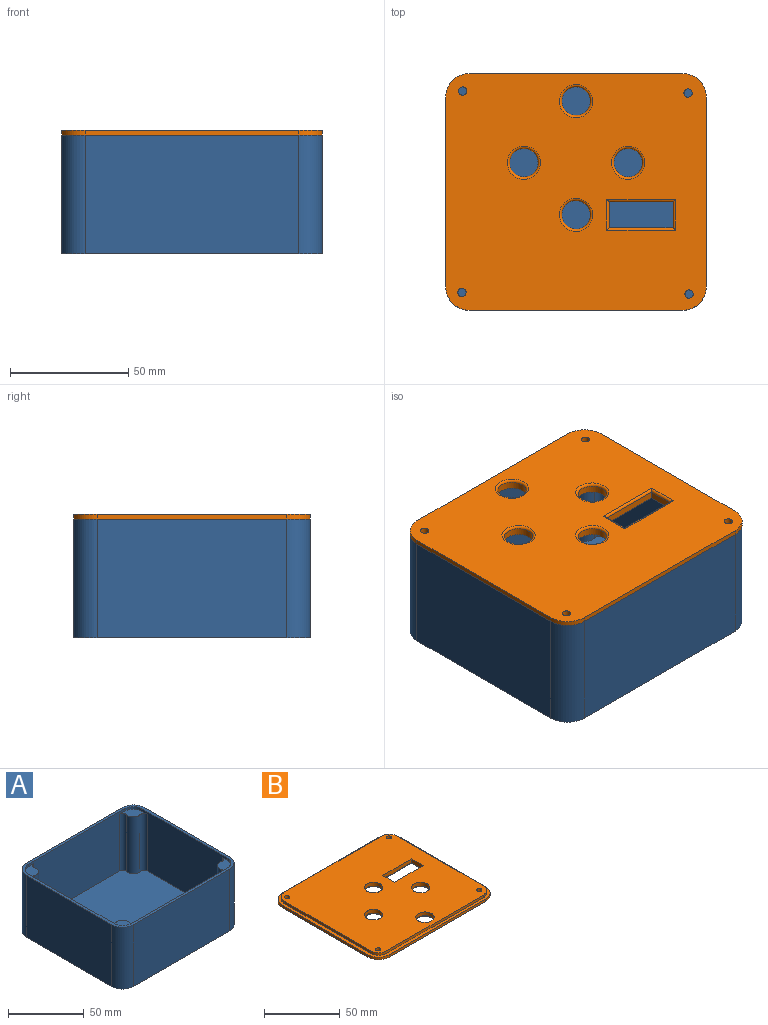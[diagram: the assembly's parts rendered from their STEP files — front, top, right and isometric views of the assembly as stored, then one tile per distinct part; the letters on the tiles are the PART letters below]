
ASSEMBLY  parts=2 mates=1
PART A: 35 faces, bbox 110x100x50 mm
  f0: cylinder r=8mm len=8mm, axis (0,0,-1), area 25.1mm2, adj f2,f13,f14,f29
  f1: cylinder r=8mm len=8mm, axis (0,0,-1), area 25.1mm2, adj f2,f16,f17,f19
  f2: plane 110x100mm, normal (0,0,1), area 793.1mm2, adj f0,f1,f3,f4,f5,f6,f7,f8
  f3: cylinder r=10mm len=50mm, axis (0,0,-1), area 785.4mm2, adj f2,f4,f10,f11
  f4: plane 90x50mm, normal (0,-1,0), area 4500mm2, adj f2,f3,f5,f11
  f5: cylinder r=10mm len=50mm, axis (0,0,-1), area 785.4mm2, adj f2,f4,f6,f11
  f6: plane 80x50mm, normal (1,0,0), area 4000mm2, adj f2,f5,f7,f11
  f7: cylinder r=10mm len=50mm, axis (0,0,-1), area 785.4mm2, adj f2,f6,f8,f11
  f8: plane 90x50mm, normal (0,1,0), area 4500mm2, adj f2,f7,f9,f11
  f9: cylinder r=10mm len=50mm, axis (0,0,-1), area 785.4mm2, adj f2,f8,f10,f11
  f10: plane 80x50mm, normal (-1,0,0), area 4000mm2, adj f2,f3,f9,f11
  f11: plane 110x100mm, normal (0,0,-1), area 10914.2mm2, adj f3,f4,f5,f6,f7,f8,f9,f10
  f12: cylinder r=8mm len=8mm, axis (0,0,-1), area 25.1mm2, adj f2,f13,f17,f27
  f13: plane 90x48mm, normal (0,1,0), area 3871.8mm2, adj f0,f2,f12,f18,f27,f29,f31,f34
  f14: plane 80x48mm, normal (-1,0,0), area 3391.8mm2, adj f0,f2,f15,f18,f23,f26,f29,f32
  f15: cylinder r=8mm len=8mm, axis (0,0,-1), area 25.1mm2, adj f2,f14,f16,f23
  f16: plane 90x48mm, normal (0,-1,0), area 3871.8mm2, adj f1,f2,f15,f18,f19,f21,f23,f25
  f17: plane 80x48mm, normal (1,0,0), area 3391.8mm2, adj f1,f2,f12,f18,f19,f22,f27,f33
  f18: plane 106x96mm, normal (0,0,1), area 9777.8mm2, adj f13,f14,f16,f17,f20,f21,f22,f24
  f19: plane 12.87x12.87mm, normal (0,0,1), area 85.8mm2, adj f1,f16,f17,f20,f21,f22
  f20: cylinder r=5mm len=46mm, axis (0,0,-1), area 487.7mm2, adj f18,f19,f21,f22
  f21: cylinder r=3mm len=46mm, axis (0,0,-1), area 254.7mm2, adj f16,f18,f19,f20
  f22: cylinder r=3mm len=46mm, axis (0,0,-1), area 254.7mm2, adj f17,f18,f19,f20
  f23: plane 12.87x12.87mm, normal (0,0,1), area 85.8mm2, adj f14,f15,f16,f24,f25,f26
  f24: cylinder r=5mm len=46mm, axis (0,0,-1), area 487.7mm2, adj f18,f23,f25,f26
  f25: cylinder r=3mm len=46mm, axis (0,0,-1), area 254.7mm2, adj f16,f18,f23,f24
  f26: cylinder r=3mm len=46mm, axis (0,0,-1), area 254.7mm2, adj f14,f18,f23,f24
  f27: plane 12.87x12.87mm, normal (0,0,1), area 85.8mm2, adj f12,f13,f17,f28,f33,f34
  f28: cylinder r=5mm len=46mm, axis (0,0,-1), area 487.7mm2, adj f18,f27,f33,f34
  f29: plane 12.87x12.87mm, normal (0,0,1), area 85.8mm2, adj f0,f13,f14,f30,f31,f32
  f30: cylinder r=5mm len=46mm, axis (0,0,-1), area 487.7mm2, adj f18,f29,f31,f32
  f31: cylinder r=3mm len=46mm, axis (0,0,-1), area 254.7mm2, adj f13,f18,f29,f30
  f32: cylinder r=3mm len=46mm, axis (0,0,-1), area 254.7mm2, adj f14,f18,f29,f30
  f33: cylinder r=3mm len=46mm, axis (0,0,-1), area 254.7mm2, adj f17,f18,f27,f28
  f34: cylinder r=3mm len=46mm, axis (0,0,-1), area 254.7mm2, adj f13,f18,f27,f28
PART B: 39 faces, bbox 110x100x4 mm
  f0: plane 110x100mm, normal (0,0,-1), area 9882.9mm2, adj f2,f3,f4,f5,f6,f7,f8,f9
  f1: plane 105.4x95.4mm, normal (0,0,1), area 9216.4mm2, adj f11,f12,f13,f14,f15,f16,f17,f18
  f2: plane 90x2mm, normal (0,1,0), area 180mm2, adj f0,f3,f9,f10
  f3: cylinder r=10mm len=10mm, axis (0,0,1), area 31.4mm2, adj f0,f2,f4,f10
  f4: plane 80x2mm, normal (-1,0,0), area 160mm2, adj f0,f3,f5,f10
  f5: cylinder r=10mm len=10mm, axis (0,0,1), area 31.4mm2, adj f0,f4,f6,f10
  f6: plane 90x2mm, normal (0,-1,0), area 180mm2, adj f0,f5,f7,f10
  f7: cylinder r=10mm len=10mm, axis (0,0,1), area 31.4mm2, adj f0,f6,f8,f10
  f8: plane 80x2mm, normal (1,0,0), area 160mm2, adj f0,f7,f9,f10
  f9: cylinder r=10mm len=10mm, axis (0,0,1), area 31.4mm2, adj f0,f2,f8,f10
  f10: plane 110x100mm, normal (0,0,1), area 909.9mm2, adj f2,f3,f4,f5,f6,f7,f8,f9
  f11: plane 90x2mm, normal (0,1,0), area 180mm2, adj f1,f10,f12,f18
  f12: cylinder r=7.7mm len=7.7mm, axis (0,0,-1), area 24.2mm2, adj f1,f10,f11,f13
  f13: plane 80x2mm, normal (-1,0,0), area 160mm2, adj f1,f10,f12,f14
  f14: cylinder r=7.7mm len=7.7mm, axis (0,0,-1), area 24.2mm2, adj f1,f10,f13,f15
  f15: plane 90x2mm, normal (0,-1,0), area 180mm2, adj f1,f10,f14,f16
  f16: cylinder r=7.7mm len=7.7mm, axis (0,0,-1), area 24.2mm2, adj f1,f10,f15,f17
  f17: plane 80x2mm, normal (1,0,0), area 160mm2, adj f1,f10,f16,f18
  f18: cylinder r=7.7mm len=7.7mm, axis (0,0,-1), area 24.2mm2, adj f1,f10,f11,f17
  f19: cylinder r=6mm len=12mm, axis (0,0,1), area 113.1mm2, adj f1,f34
  f20: cylinder r=6mm len=12mm, axis (0,0,1), area 113.1mm2, adj f1,f33
  f21: cylinder r=6mm len=12mm, axis (0,0,1), area 113.1mm2, adj f1,f32
  f22: plane 27x3mm, normal (0,-1,0), area 81mm2, adj f1,f23,f25,f31
  f23: plane 11x3mm, normal (1,0,0), area 33mm2, adj f1,f22,f24,f29
  f24: plane 27x3mm, normal (0,1,0), area 81mm2, adj f1,f23,f25,f28
  f25: plane 11x3mm, normal (-1,0,0), area 33mm2, adj f1,f22,f24,f30
  f26: cylinder r=6mm len=12mm, axis (0,0,1), area 113.1mm2, adj f1,f27
  f27: torus R=7mm, axis (0,0,1), area 62.8mm2, adj f0,f26
  f28: cylinder r=1mm len=29mm, axis (1,0,0), area 43.6mm2, adj f0,f24,f29,f30
  f29: cylinder r=1mm len=13mm, axis (0,-1,0), area 18.4mm2, adj f0,f23,f28,f31
  f30: cylinder r=1mm len=13mm, axis (0,1,0), area 18.4mm2, adj f0,f25,f28,f31
  f31: cylinder r=1mm len=29mm, axis (-1,0,0), area 43.6mm2, adj f0,f22,f29,f30
  f32: torus R=7mm, axis (0,0,1), area 62.8mm2, adj f0,f21
  f33: torus R=7mm, axis (0,0,1), area 62.8mm2, adj f0,f20
  f34: torus R=7mm, axis (0,0,1), area 62.8mm2, adj f0,f19
  f35: cylinder r=1.75mm len=4mm, axis (0,0,1), area 44mm2, adj f0,f1
  f36: cylinder r=1.75mm len=4mm, axis (0,0,1), area 44mm2, adj f0,f1
  f37: cylinder r=1.75mm len=4mm, axis (0,0,1), area 44mm2, adj f0,f1
  f38: cylinder r=1.75mm len=4mm, axis (0,0,1), area 44mm2, adj f0,f1
PLACE A t=(-98.18,-108.78,-75.77)mm
PLACE B rot(axis=(1,0,0),180deg) t=(-98.18,-8.78,-25.77)mm
MATE planar B.f10 <-> A.f2  axis (0,0,-1) through (-43.18,-58.78,-25.77)mm
